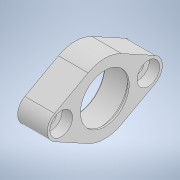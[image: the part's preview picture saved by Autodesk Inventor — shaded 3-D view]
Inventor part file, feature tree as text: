
AUTODESK INVENTOR PART (.ipt)
format: ipt  version: 2022 (Build 260153000, 153)  size: 165,888 bytes
history: native  units: in
note: dims shown in document units (in); Inventor stores cm internally (conversion verified against a paired STEP export)
features: other x3, extrude x2, sketch x2, chamfer x1, projected_geometry x1
ambient origin geometry x8: Origin, YZ Plane, XZ Plane, XY Plane, X Axis, Y Axis, Z Axis, Center Point
bodies: Solid1 (feature_tree)
feature tree (9):
  other  "XY Drive Bearing Holder.ipt"
  extrude  "Extrusion1"  Depth=0.1181in TaperAngle=0.0deg
  chamfer  "Chamfer1"  Distance=0.0197in Angle=45.0deg
  extrude  "Extrusion2"  [1 undecoded]
  other  "Solid3::XY Drive Bearing Holder.ipt"
  other  "TaggingFeature1"
  sketch  "Sketch1"  dims[d0=0.3937in d1=0.1181in d2=0.0in d3=0.0197in d4=0.125in d5=45.0deg]
  sketch  "Sketch2"  dims[d6=0.1181in d7=0.0in]
  projected_geometry  "Projected Loop1"
note: 1 required parameter value undecoded (feature->parameter linkage not recoverable at this tier; creation-order binding heuristic only, values carry confidence <= 0.55)
